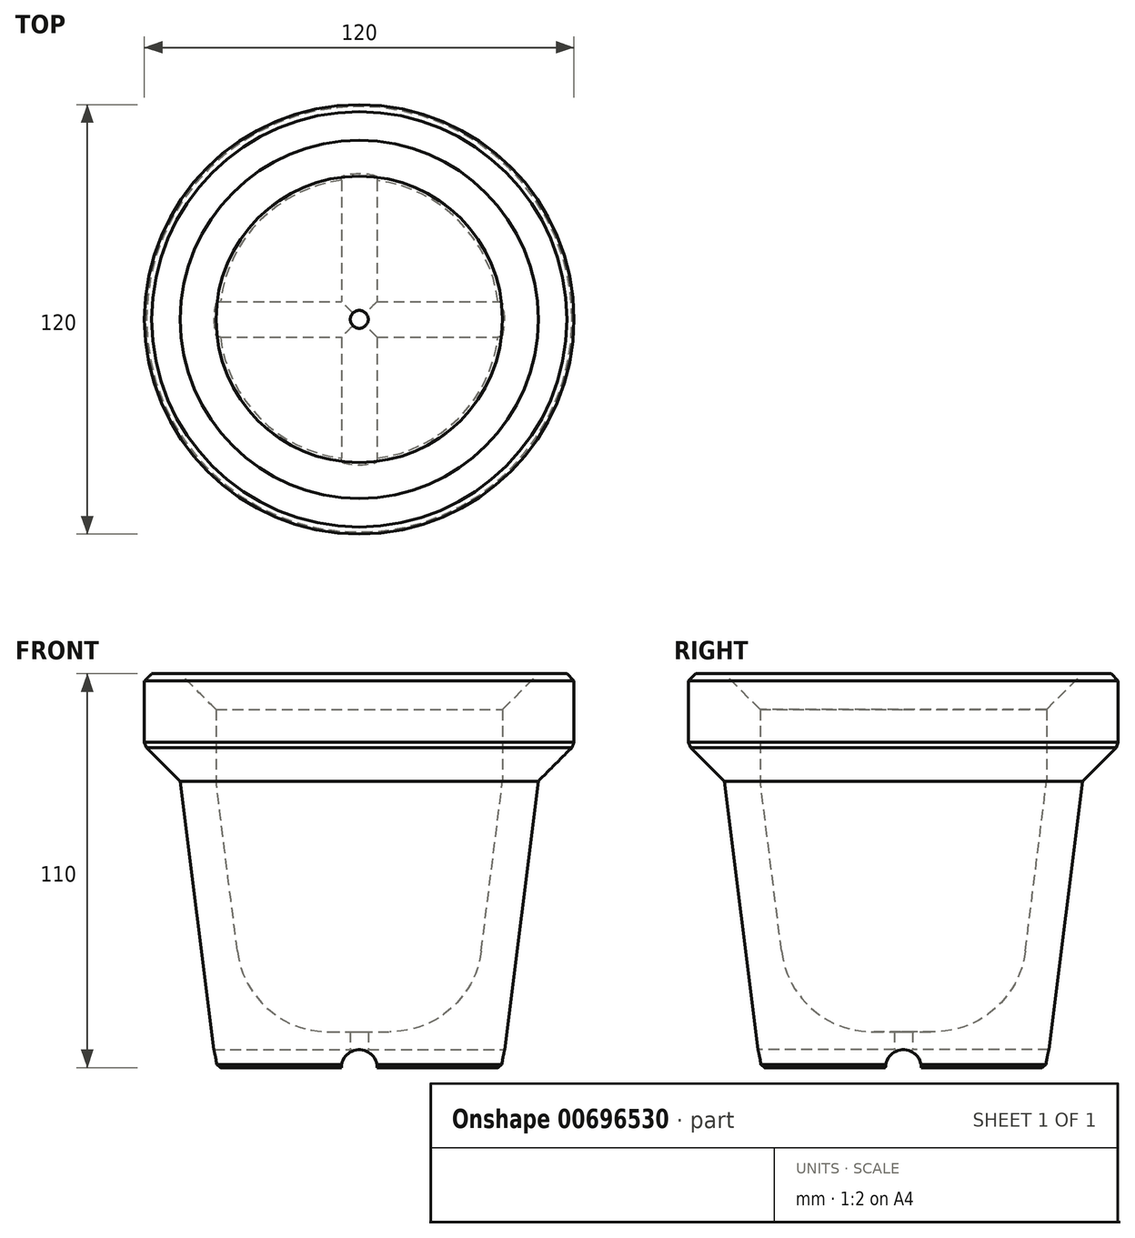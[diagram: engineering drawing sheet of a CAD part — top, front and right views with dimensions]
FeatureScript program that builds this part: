
annotation { "Feature Type Name" : "Feature", "Feature Type Description" : "" }
export const myFeature = defineFeature(function(context is Context, id is Id, definition is map)
    precondition{}
    {
        {
            var Q0;
            Q0=qCreatedBy(makeId("Front.planeOp"),FACE);
            var sketch = newSketch(context, id + "F0", { "sketchPlane" : qUnion([Q0])});
            skLineSegment(sketch, "E0.bottom", {"start": v(0, 0) * mm, "end": v(60, 0) * mm, "construction": true});
            skLineSegment(sketch, "E0.top", {"start": v(0, 110) * mm, "end": v(60, 110) * mm, "construction": true});
            skLineSegment(sketch, "E0.left", {"start": v(0, 0) * mm, "end": v(0, 110) * mm, "construction": true});
            skLineSegment(sketch, "E0.right", {"start": v(60, 0) * mm, "end": v(60, 110) * mm, "construction": true});
            skLineSegment(sketch, "E1", {"start": v(0, 0) * mm, "end": v(40, 0) * mm, "construction": true});
            skLineSegment(sketch, "E2", {"start": v(60, 110) * mm, "end": v(60, 80) * mm, "construction": true});
            skLineSegment(sketch, "E3.bottom", {"start": v(60, 110) * mm, "end": v(50, 110) * mm});
            skLineSegment(sketch, "E3.top", {"start": v(60, 80) * mm, "end": v(50, 80) * mm});
            skLineSegment(sketch, "E3.left", {"start": v(60, 110) * mm, "end": v(60, 80) * mm});
            skLineSegment(sketch, "E3.right", {"start": v(50, 110) * mm, "end": v(50, 80) * mm});
            skLineSegment(sketch, "E4", {"start": v(50, 80) * mm, "end": v(40, 0) * mm});
            skLineSegment(sketch, "E5.bottom", {"start": v(0, 0) * mm, "end": v(41.25, 0) * mm});
            skLineSegment(sketch, "E5.top", {"start": v(0, 10) * mm, "end": v(41.25, 10) * mm});
            skLineSegment(sketch, "E5.left", {"start": v(0, 0) * mm, "end": v(0, 10) * mm});
            skLineSegment(sketch, "E5.right", {"start": v(41.25, 0) * mm, "end": v(41.25, 10) * mm});
            skLineSegment(sketch, "E6", {"start": v(50, 110) * mm, "end": v(40, 110) * mm, "construction": true});
            skLineSegment(sketch, "E7", {"start": v(50, 80) * mm, "end": v(40, 80) * mm, "construction": true});
            skLineSegment(sketch, "E8", {"start": v(41.25, 10) * mm, "end": v(31.25, 10) * mm, "construction": true});
            skLineSegment(sketch, "E9", {"start": v(40, 110) * mm, "end": v(40, 80) * mm});
            skLineSegment(sketch, "E10", {"start": v(40, 80) * mm, "end": v(31.25, 10) * mm});
            skLineSegment(sketch, "E11", {"start": v(40, 110) * mm, "end": v(50, 110) * mm});
            skSolve(sketch);
        }
        {
            var Q0;
            {var subQ4=sQuery(id+"F0.wireOp",EDGE,"E5.left");Q0=makeQuery(id+"F0.imprint","IMPRINT",FACE,{"disambiguationData":[TD([[makeQuery(id+"F0.imprint","IMPRINT",EDGE,{"derivedFrom":subQ4}),-1.0]])]});}
            var Q1;
            {var subQ4=sQuery(id+"F0.wireOp",EDGE,"E3.right");Q1=makeQuery(id+"F0.imprint","IMPRINT",FACE,{"disambiguationData":[TD([[makeQuery(id+"F0.imprint","IMPRINT",EDGE,{"derivedFrom":subQ4}),-1.0]])]});}
            var Q2;
            Q2=makeQuery(id+"F0.imprint","IMPRINT",FACE,{"disambiguationData":[TD([[makeQuery(id+"F0.imprint","IMPRINT",EDGE,{"derivedFrom":sQuery(id+"F0.wireOp",EDGE,"E3.bottom")}),1.0]])]});
            var Q3;
            Q3=sQuery(id+"F0.wireOp",EDGE,"E0.left");
            revolve(context, id + "F1", {"entities" : qUnion([Q0, Q1, Q2]), "axis" : qUnion([Q3]), "revolveType" : RevolveType.FULL});
        }
        {
            var Q0;
            Q0=makeQuery(id+"F1.opRevolve","SWEPT_EDGE",EDGE,{"disambiguationData":[OSD([sQuery(id+"F0.wireOp",EDGE,"E3.top"),sQuery(id+"F0.wireOp",EDGE,"E3.left")])]});
            chamfer(context, id + "F2", {"entities" : qUnion([Q0]), "width" : 10 * mm, "tangentPropagation" : true});
        }
        {
            var Q0;
            Q0=makeQuery(id+"F1.opRevolve","SWEPT_EDGE",EDGE,{"disambiguationData":[OSD([sQuery(id+"F0.wireOp",EDGE,"E9"),sQuery(id+"F0.wireOp",EDGE,"E11")])]});
            chamfer(context, id + "F3", {"entities" : qUnion([Q0]), "width" : 10 * mm, "tangentPropagation" : true});
        }
        {
            var Q0;
            Q0=makeQuery(id+"F1.opRevolve","SWEPT_EDGE",EDGE,{"disambiguationData":[OSD([sQuery(id+"F0.wireOp",EDGE,"E3.bottom"),sQuery(id+"F0.wireOp",EDGE,"E3.left")])]});
            var Q1;
            {var subQ0=sQuery(id+"F0.wireOp",EDGE,"E3.left");Q1=makeQuery(id+"F2.opChamfer","BLEND_EDGE",EDGE,{"blendedFrom":[makeQuery(id+"F1.opRevolve","SWEPT_EDGE",EDGE,{"disambiguationData":[OSD([sQuery(id+"F0.wireOp",EDGE,"E3.top"),subQ0])]}),makeQuery(id+"F1.opRevolve","SWEPT_FACE",FACE,{"disambiguationData":[OSD([subQ0])]})],"blendedInto":[makeQuery(id+"F1.opRevolve","SWEPT_FACE",FACE,{"disambiguationData":[OSD([subQ0])]})]});}
            chamfer(context, id + "F4", {"entities" : qUnion([Q0, Q1]), "width" : 2 * mm, "tangentPropagation" : true});
        }
        {
            var Q0;
            Q0=makeQuery(id+"F1.opRevolve","SWEPT_EDGE",EDGE,{"disambiguationData":[OSD([sQuery(id+"F0.wireOp",EDGE,"E4"),sQuery(id+"F0.wireOp",EDGE,"E5.bottom")])]});
            chamfer(context, id + "F5", {"entities" : qUnion([Q0]), "width" : 1 * mm, "tangentPropagation" : true});
        }
        {
            var Q0;
            Q0=qCreatedBy(makeId("Front.planeOp"),FACE);
            var sketch = newSketch(context, id + "F6", { "sketchPlane" : qUnion([Q0])});
            skCircle(sketch, "E12", {"center": v(0, 0) * mm, "radius": 5 * mm});
            skSolve(sketch);
        }
        {
            var Q0;
            Q0=makeQuery(id+"F6.imprint","IMPRINT",FACE,{"disambiguationData":[TD([[makeQuery(id+"F6.imprint","IMPRINT",EDGE,{"derivedFrom":sQuery(id+"F6.wireOp",EDGE,"E12")}),1.0]])]});
            extrude(context, id + "F7", {"entities" : qUnion([Q0]), "operationType" : NewBodyOperationType.REMOVE, "oppositeDirection" : true, "depth" : 100 * mm, "offsetDistance" : 25 * mm, "hasSecondDirection" : true, "secondDirectionOppositeDirection" : false, "secondDirectionDepth" : 100 * mm});
        }
        {
            var Q0;
            Q0=qCreatedBy(makeId("Right.planeOp"),FACE);
            var sketch = newSketch(context, id + "F8", { "sketchPlane" : qUnion([Q0])});
            skCircle(sketch, "E13", {"center": v(0, 0) * mm, "radius": 5 * mm});
            skSolve(sketch);
        }
        {
            var Q0;
            Q0 = qSketchRegion(id + "F8", true);
            var Q1;
            Q1=sQuery(id+"F8.wireOp",EDGE,"E13");
            extrude(context, id + "F9", {"entities" : qUnion([Q0]), "operationType" : NewBodyOperationType.REMOVE, "surfaceEntities" : qUnion([Q1]), "oppositeDirection" : true, "depth" : 100 * mm, "offsetDistance" : 25 * mm, "hasSecondDirection" : true, "secondDirectionOppositeDirection" : false, "secondDirectionDepth" : 100 * mm});
        }
        {
            var Q0;
            Q0=qCreatedBy(makeId("Top.planeOp"),FACE);
            var sketch = newSketch(context, id + "F10", { "sketchPlane" : qUnion([Q0])});
            skCircle(sketch, "E14", {"center": v(0, 0) * mm, "radius": 2.5 * mm});
            skSolve(sketch);
        }
        {
            var Q0;
            Q0 = qSketchRegion(id + "F10", true);
            var Q1;
            Q1=sQuery(id+"F10.wireOp",EDGE,"E14");
            extrude(context, id + "F11", {"entities" : qUnion([Q0]), "operationType" : NewBodyOperationType.REMOVE, "surfaceEntities" : qUnion([Q1]), "depth" : 25 * mm, "offsetDistance" : 25 * mm});
        }
        {
            var Q0;
            Q0=makeQuery(id+"F1.opRevolve","SWEPT_EDGE",EDGE,{"disambiguationData":[OSD([sQuery(id+"F0.wireOp",EDGE,"E5.top"),sQuery(id+"F0.wireOp",EDGE,"E10")])]});
            fillet(context, id + "F12", {"entities" : qUnion([Q0]), "radius" : 25.76 * mm, "tangentPropagation" : true, "allowEdgeOverflow" : false});
        }
    });
